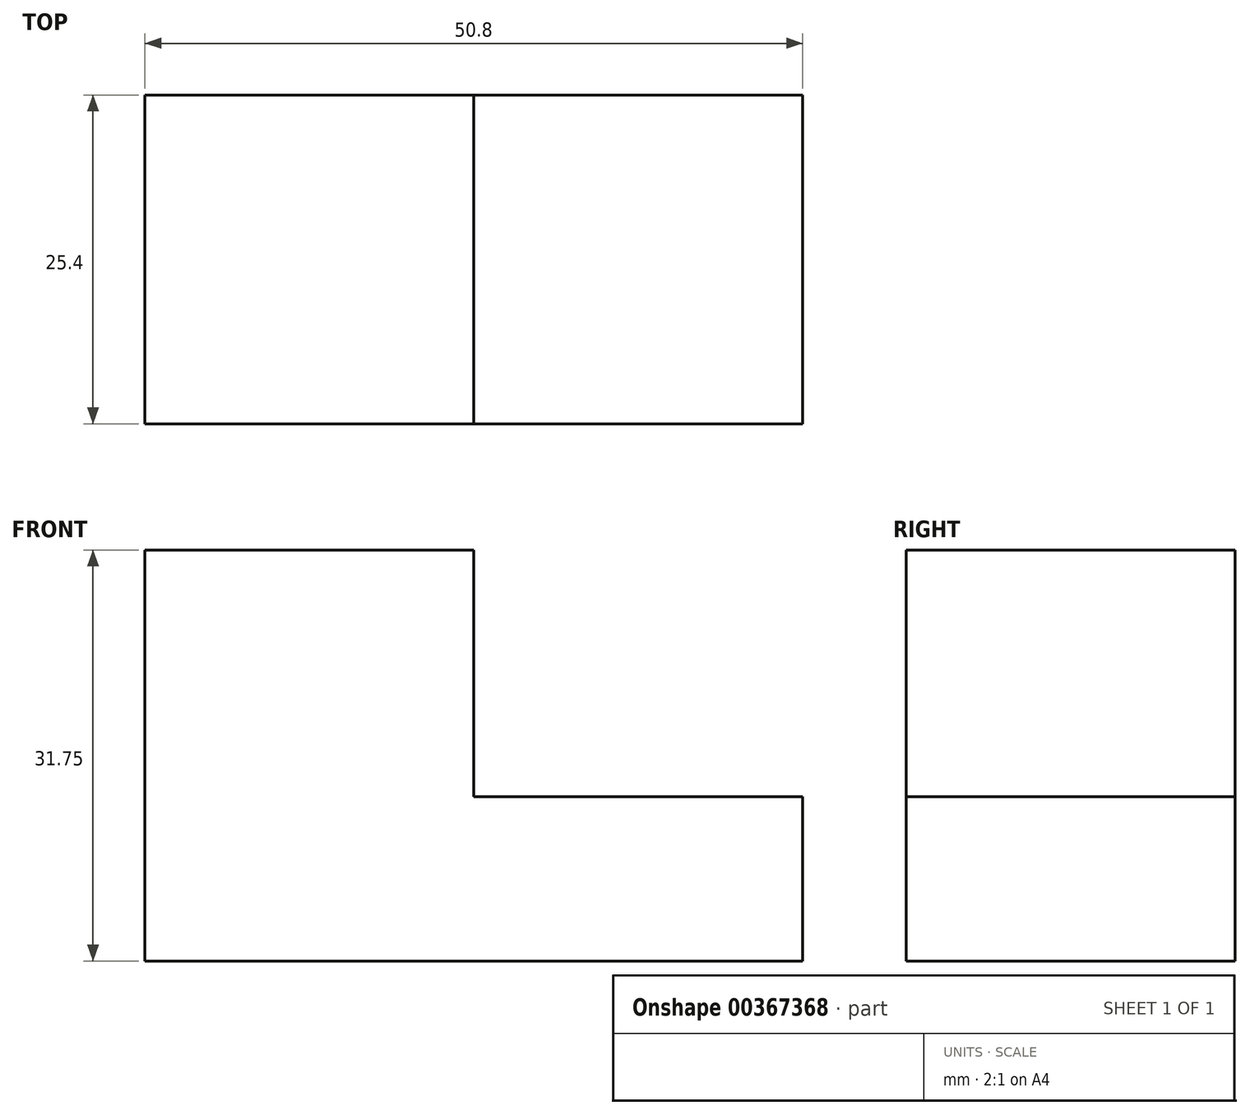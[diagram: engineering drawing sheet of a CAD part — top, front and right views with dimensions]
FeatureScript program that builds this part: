
annotation { "Feature Type Name" : "Feature", "Feature Type Description" : "" }
export const myFeature = defineFeature(function(context is Context, id is Id, definition is map)
    precondition{}
    {
        {
            var Q0;
            Q0=qCreatedBy(makeId("Front.planeOp"),FACE);
            var sketch = newSketch(context, id + "F0", { "sketchPlane" : qUnion([Q0])});
            skLineSegment(sketch, "E0", {"start": v(0, 31.75) * mm, "end": v(0, 0) * mm});
            skLineSegment(sketch, "E1", {"start": v(0, 0) * mm, "end": v(50.8, 0) * mm});
            skLineSegment(sketch, "E2", {"start": v(50.8, 12.7) * mm, "end": v(50.8, 0) * mm});
            skLineSegment(sketch, "E3", {"start": v(50.8, 12.7) * mm, "end": v(25.4, 12.7) * mm});
            skLineSegment(sketch, "E4", {"start": v(25.4, 12.7) * mm, "end": v(25.4, 31.75) * mm});
            skLineSegment(sketch, "E5", {"start": v(25.4, 31.75) * mm, "end": v(0, 31.75) * mm});
            skSolve(sketch);
        }
        {
            var Q0;
            Q0=makeQuery(id+"F0.imprint","IMPRINT",FACE,{"disambiguationData":[TD([[makeQuery(id+"F0.imprint","IMPRINT",EDGE,{"derivedFrom":sQuery(id+"F0.wireOp",EDGE,"E0")}),1.0]])]});
            extrude(context, id + "F1", {"entities" : qUnion([Q0]), "depth" : 25.4 * mm});
        }
    });
